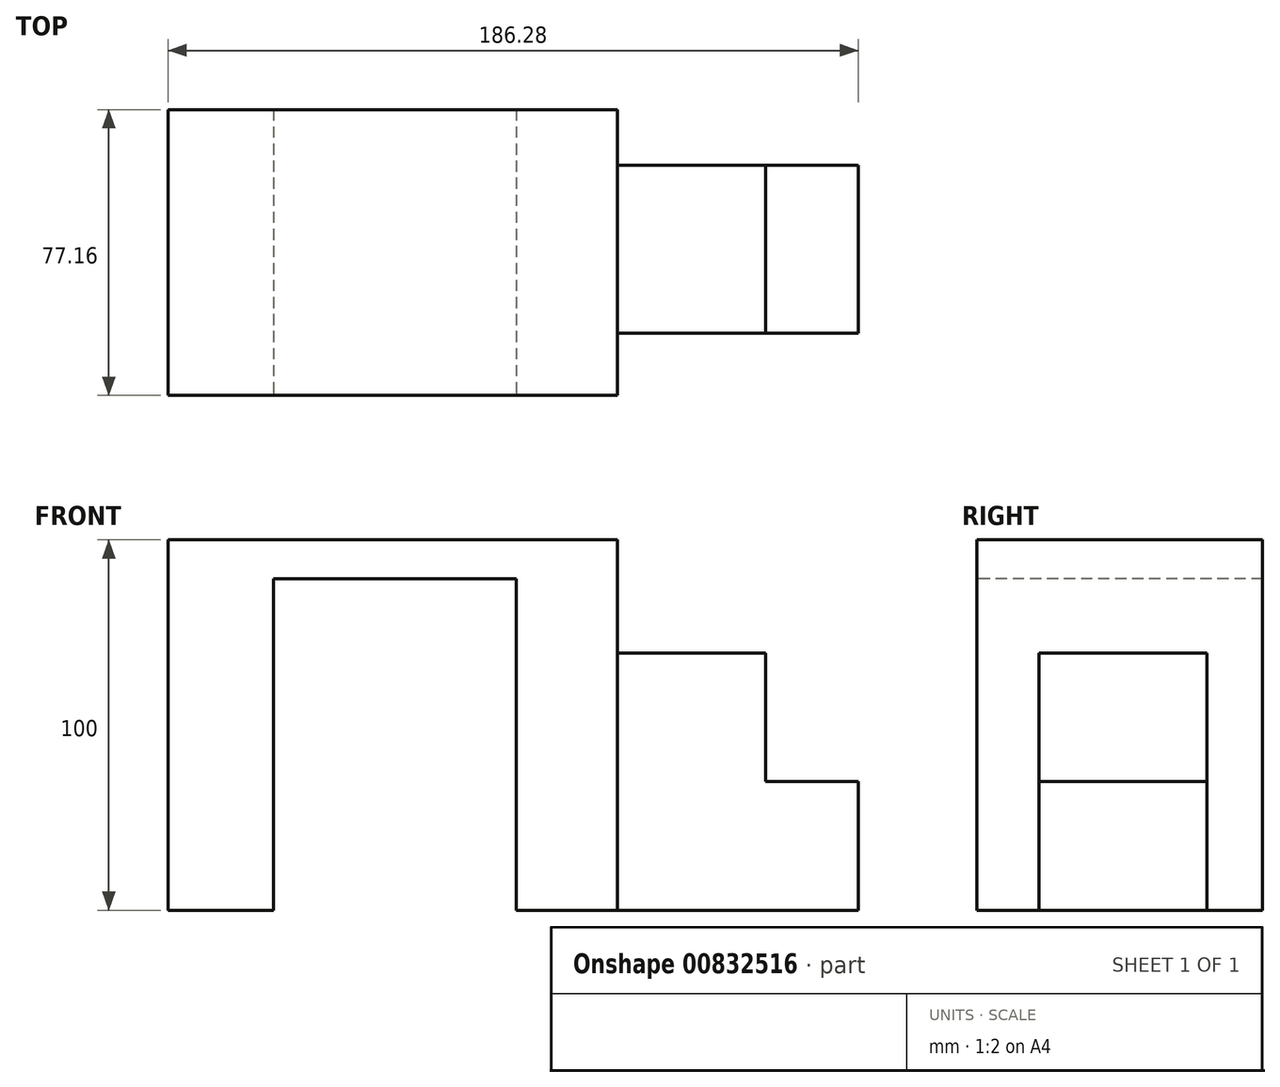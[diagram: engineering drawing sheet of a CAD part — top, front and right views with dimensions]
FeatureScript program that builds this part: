
annotation { "Feature Type Name" : "Feature", "Feature Type Description" : "" }
export const myFeature = defineFeature(function(context is Context, id is Id, definition is map)
    precondition{}
    {
        {
            var Q0;
            Q0=qCreatedBy(makeId("Top.planeOp"),FACE);
            var sketch = newSketch(context, id + "F0", { "sketchPlane" : qUnion([Q0])});
            skLineSegment(sketch, "E0.bottom", {"start": v(0, 0) * mm, "end": v(-121.28, 0) * mm});
            skLineSegment(sketch, "E0.top", {"start": v(0, -37.16) * mm, "end": v(-121.28, -37.16) * mm});
            skLineSegment(sketch, "E0.left", {"start": v(0, 0) * mm, "end": v(0, -37.16) * mm});
            skLineSegment(sketch, "E0.right", {"start": v(-121.28, 0) * mm, "end": v(-121.28, -37.16) * mm});
            skSolve(sketch);
        }
        {
            var Q0;
            Q0 = qSketchRegion(id + "F0", true);
            extrude(context, id + "F1", {"entities" : qUnion([Q0]), "depth" : 100 * mm, "offsetDistance" : 25 * mm});
        }
        {
            var Q0;
            Q0=makeQuery(id+"F1.opExtrude","SWEPT_FACE",FACE,{"disambiguationData":[OSD([sQuery(id+"F0.wireOp",EDGE,"E0.top")])]});
            extrude(context, id + "F2", {"entities" : qUnion([Q0]), "operationType" : NewBodyOperationType.ADD, "depth" : 25 * mm, "offsetDistance" : 25 * mm});
        }
        {
            var Q0;
            Q0=makeQuery(id+"F2.opExtrude","CAP_FACE",FACE,{"disambiguationData":[OSD([sQuery(id+"F0.wireOp",EDGE,"E0.top")])],"isStart":false});
            extrude(context, id + "F3", {"entities" : qUnion([Q0]), "operationType" : NewBodyOperationType.ADD, "depth" : 15 * mm, "offsetDistance" : 25 * mm});
        }
        {
            var Q0;
            Q0=makeQuery(id+"F3.opExtrude","CAP_FACE",FACE,{"disambiguationData":[OSD([sQuery(id+"F0.wireOp",EDGE,"E0.top")])],"isStart":false});
            var sketch = newSketch(context, id + "F4", { "sketchPlane" : qUnion([Q0])});
            skLineSegment(sketch, "E1.bottom", {"start": v(-92.9, 0) * mm, "end": v(-27.32, 0) * mm});
            skLineSegment(sketch, "E1.top", {"start": v(-92.9, 89.45) * mm, "end": v(-27.32, 89.45) * mm});
            skLineSegment(sketch, "E1.left", {"start": v(-92.9, 0) * mm, "end": v(-92.9, 89.45) * mm});
            skLineSegment(sketch, "E1.right", {"start": v(-27.32, 0) * mm, "end": v(-27.32, 89.45) * mm});
            skSolve(sketch);
        }
        {
            var Q0;
            Q0=makeQuery(id+"F4.imprint","IMPRINT",FACE,{"disambiguationData":[TD([[makeQuery(id+"F4.imprint","IMPRINT",EDGE,{"derivedFrom":sQuery(id+"F4.wireOp",EDGE,"E1.bottom")}),-1.0]])]});
            extrude(context, id + "F5", {"entities" : qUnion([Q0]), "operationType" : NewBodyOperationType.REMOVE, "oppositeDirection" : true, "depth" : 1200 * mm, "offsetDistance" : 25 * mm});
        }
        {
            var Q0;
            Q0=makeQuery(id+"F5.boolean.opBoolean","COPY",FACE,{"derivedFrom":makeQuery(id+"F5.opExtrude","CAP_FACE",FACE,{"disambiguationData":[OSD([sQuery(id+"F4.wireOp",EDGE,"E1.bottom"),sQuery(id+"F4.wireOp",EDGE,"E1.top"),sQuery(id+"F4.wireOp",EDGE,"E1.left"),sQuery(id+"F4.wireOp",EDGE,"E1.right")])],"isStart":false})});
            var sketch = newSketch(context, id + "F6", { "sketchPlane" : qUnion([Q0])});
            skSolve(sketch);
        }
        {
            var Q0;
            {var subQ0=sQuery(id+"F0.wireOp",EDGE,"E0.left");var subQ1=sQuery(id+"F0.wireOp",EDGE,"E0.top");Q0=makeQuery(id+"F3.boolean.opBoolean","MERGE",FACE,{"derivedFrom":[makeQuery(id+"F2.boolean.opBoolean","MERGE",FACE,{"derivedFrom":[makeQuery(id+"F1.opExtrude","SWEPT_FACE",FACE,{"disambiguationData":[OSD([subQ0])]}),makeQuery(id+"F2.opExtrude","SWEPT_FACE",FACE,{"disambiguationData":[OSD([subQ1,subQ0])]})]}),makeQuery(id+"F3.opExtrude","SWEPT_FACE",FACE,{"disambiguationData":[OSD([subQ1,subQ0])]})]});}
            var sketch = newSketch(context, id + "F7", { "sketchPlane" : qUnion([Q0])});
            skLineSegment(sketch, "E2.bottom", {"start": v(-60.4, 0) * mm, "end": v(-15.05, 0) * mm});
            skLineSegment(sketch, "E2.top", {"start": v(-60.4, 69.37) * mm, "end": v(-15.05, 69.37) * mm});
            skLineSegment(sketch, "E2.left", {"start": v(-60.4, 0) * mm, "end": v(-60.4, 69.37) * mm});
            skLineSegment(sketch, "E2.right", {"start": v(-15.05, 0) * mm, "end": v(-15.05, 69.37) * mm});
            skSolve(sketch);
        }
        {
            var Q0;
            Q0 = qSketchRegion(id + "F7", true);
            extrude(context, id + "F8", {"entities" : qUnion([Q0]), "operationType" : NewBodyOperationType.ADD, "depth" : 40 * mm, "offsetDistance" : 25 * mm});
        }
        {
            var Q0;
            Q0=makeQuery(id+"F8.opExtrude","CAP_FACE",FACE,{"disambiguationData":[OSD([sQuery(id+"F7.wireOp",EDGE,"E2.bottom"),sQuery(id+"F7.wireOp",EDGE,"E2.top"),sQuery(id+"F7.wireOp",EDGE,"E2.left"),sQuery(id+"F7.wireOp",EDGE,"E2.right")])],"isStart":false});
            var sketch = newSketch(context, id + "F9", { "sketchPlane" : qUnion([Q0])});
            skLineSegment(sketch, "E3.bottom", {"start": v(-60.4, 0) * mm, "end": v(-15.05, 0) * mm});
            skLineSegment(sketch, "E3.top", {"start": v(-60.4, 34.69) * mm, "end": v(-15.05, 34.69) * mm});
            skLineSegment(sketch, "E3.left", {"start": v(-60.4, 0) * mm, "end": v(-60.4, 34.69) * mm});
            skLineSegment(sketch, "E3.right", {"start": v(-15.05, 0) * mm, "end": v(-15.05, 34.69) * mm});
            skSolve(sketch);
        }
        {
            var Q0;
            Q0 = qSketchRegion(id + "F9", true);
            extrude(context, id + "F10", {"entities" : qUnion([Q0]), "operationType" : NewBodyOperationType.ADD, "depth" : 25 * mm, "offsetDistance" : 25 * mm});
        }
    });
